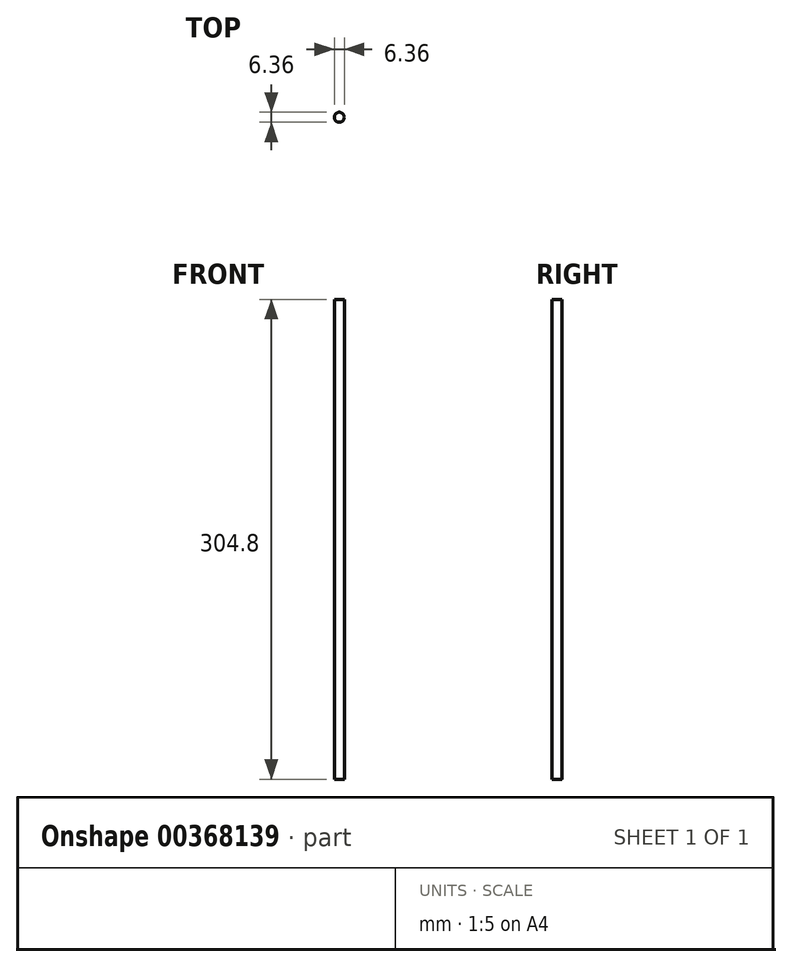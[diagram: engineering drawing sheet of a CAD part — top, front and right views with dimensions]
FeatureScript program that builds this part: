
annotation { "Feature Type Name" : "Feature", "Feature Type Description" : "" }
export const myFeature = defineFeature(function(context is Context, id is Id, definition is map)
    precondition{}
    {
        {
            var Q0;
            Q0=qCreatedBy(makeId("Top.planeOp"),FACE);
            var sketch = newSketch(context, id + "F0", { "sketchPlane" : qUnion([Q0])});
            skCircle(sketch, "E0", {"center": v(0, 0) * mm, "radius": 3.18 * mm});
            skSolve(sketch);
        }
        {
            var Q0;
            Q0 = qSketchRegion(id + "F0", true);
            extrude(context, id + "F1", {"entities" : qUnion([Q0]), "depth" : 304.8 * mm, "offsetDistance" : 25.4 * mm, "symmetric" : true});
        }
    });
